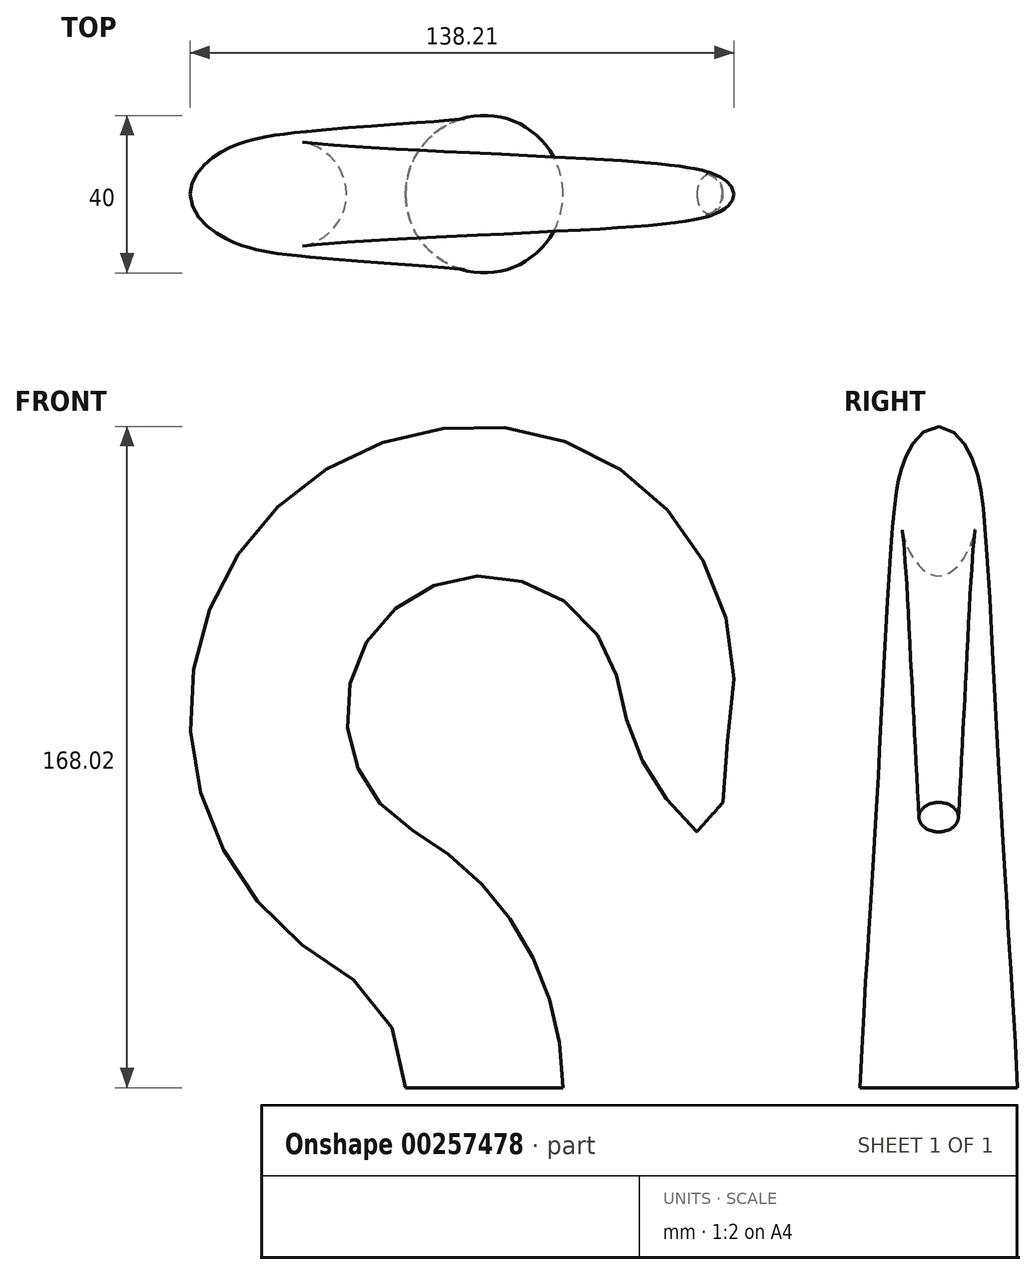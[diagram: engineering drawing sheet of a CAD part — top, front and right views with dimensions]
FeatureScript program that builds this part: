
annotation { "Feature Type Name" : "Feature", "Feature Type Description" : "" }
export const myFeature = defineFeature(function(context is Context, id is Id, definition is map)
    precondition{}
    {
        {
            var Q0;
            Q0=qCreatedBy(makeId("Front.planeOp"),FACE);
            var sketch = newSketch(context, id + "F0", { "sketchPlane" : qUnion([Q0])});
            skLineSegment(sketch, "E0", {"start": v(0, 0) * mm, "end": v(-40, 0) * mm});
            skPoint(sketch, "E1", {"position": v(-20, 0) * mm});
            skLineSegment(sketch, "E2", {"start": v(-20, 0) * mm, "end": v(-20, 168) * mm, "construction": true});
            skArc(sketch, "E3", {"start": v(-40, 0) * mm, "mid": v(-44.68, 17.48) * mm, "end": v(-57.46, 30.29) * mm});
            skArc(sketch, "E4", {"start": v(0, 0) * mm, "mid": v(-10.1, 37.58) * mm, "end": v(-37.66, 65.04) * mm});
            skLineSegment(sketch, "E5", {"start": v(-131.2, 95) * mm, "end": v(85.23, 95) * mm, "construction": true});
            skArc(sketch, "E6", {"start": v(-57.46, 30.29) * mm, "mid": v(-84.78, 57.65) * mm, "end": v(-94.77, 95) * mm});
            skArc(sketch, "E7", {"start": v(-55, 95) * mm, "mid": v(-44.75, 119.75) * mm, "end": v(-20, 130) * mm});
            skArc(sketch, "E8", {"start": v(-37.66, 65.04) * mm, "mid": v(-50.35, 77.7) * mm, "end": v(-55, 95) * mm});
            skArc(sketch, "E9", {"start": v(41.75, 88.29) * mm, "mid": v(29.83, 142.83) * mm, "end": v(-20, 168) * mm});
            skArc(sketch, "E10", {"start": v(41.75, 88.29) * mm, "mid": v(40.57, 80.43) * mm, "end": v(40.65, 72.48) * mm});
            skLineSegment(sketch, "E11", {"start": v(40.65, 72.48) * mm, "end": v(34.02, 65) * mm});
            skCircle(sketch, "E12", {"center": v(37.33, 68.74) * mm, "radius": 5 * mm, "construction": true});
            skArc(sketch, "E13", {"start": v(34.02, 65) * mm, "mid": v(21.2, 81.05) * mm, "end": v(14.57, 100.49) * mm});
            skArc(sketch, "E14", {"start": v(-20, 130) * mm, "mid": v(2.73, 121.62) * mm, "end": v(14.57, 100.49) * mm});
            skArc(sketch, "E15", {"start": v(-94.77, 95) * mm, "mid": v(-72.76, 147.25) * mm, "end": v(-20, 168) * mm});
            skSolve(sketch);
        }
        {
            var Q0;
            Q0=qCreatedBy(makeId("Top.planeOp"),FACE);
            var sketch = newSketch(context, id + "F1", { "sketchPlane" : qUnion([Q0])});
            skPoint(sketch, "E16.0", {"position": v(-20, 0) * mm});
            skPoint(sketch, "E17.0", {"position": v(-40, 0) * mm});
            skCircle(sketch, "E18", {"center": v(-20, 0) * mm, "radius": 20 * mm});
            skSolve(sketch);
        }
        {
            var Q0;
            Q0=sQuery(id+"F0.wireOp",EDGE,"E11");
            cPlane(context, id + "F2", {"entities" : qUnion([Q0]), "cplaneType" : CPlaneType.LINE_ANGLE, "offset" : 25 * mm, "angle" : 0 * degree, "width" : 150 * mm, "height" : 150 * mm});
        }
        {
            var Q0;
            Q0=qCreatedBy(id+"F2.planeOp",FACE);
            var sketch = newSketch(context, id + "F3", { "sketchPlane" : qUnion([Q0])});
            skLineSegment(sketch, "E19.0", {"start": v(0, 81.2) * mm, "end": v(0, 71.2) * mm, "construction": true});
            skCircle(sketch, "E20", {"center": v(0, 76.2) * mm, "radius": 5 * mm});
            skSolve(sketch);
        }
        {
            var Q0;
            Q0=qCreatedBy(makeId("Front.planeOp"),FACE);
            var sketch = newSketch(context, id + "F4", { "sketchPlane" : qUnion([Q0])});
            skArc(sketch, "E21.0", {"start": v(-40, 0) * mm, "mid": v(-44.68, 17.48) * mm, "end": v(-57.46, 30.29) * mm});
            skArc(sketch, "E22.0", {"start": v(-57.46, 30.29) * mm, "mid": v(-84.78, 57.65) * mm, "end": v(-94.77, 95) * mm});
            skArc(sketch, "E23.0", {"start": v(-94.77, 95) * mm, "mid": v(-72.76, 147.25) * mm, "end": v(-20, 168) * mm});
            skArc(sketch, "E24.0", {"start": v(41.75, 88.29) * mm, "mid": v(29.83, 142.83) * mm, "end": v(-20, 168) * mm});
            skArc(sketch, "E25.0", {"start": v(41.75, 88.29) * mm, "mid": v(40.57, 80.43) * mm, "end": v(40.65, 72.48) * mm});
            skSolve(sketch);
        }
        {
            var Q0;
            Q0=qCreatedBy(makeId("Front.planeOp"),FACE);
            var sketch = newSketch(context, id + "F5", { "sketchPlane" : qUnion([Q0])});
            skArc(sketch, "E26.0", {"start": v(0, 0) * mm, "mid": v(-10.1, 37.58) * mm, "end": v(-37.66, 65.04) * mm});
            skArc(sketch, "E27.0", {"start": v(-37.66, 65.04) * mm, "mid": v(-50.35, 77.7) * mm, "end": v(-55, 95) * mm});
            skArc(sketch, "E28.0", {"start": v(-55, 95) * mm, "mid": v(-44.75, 119.75) * mm, "end": v(-20, 130) * mm});
            skArc(sketch, "E29.0", {"start": v(-20, 130) * mm, "mid": v(2.73, 121.62) * mm, "end": v(14.57, 100.49) * mm});
            skArc(sketch, "E30.0", {"start": v(34.02, 65) * mm, "mid": v(21.2, 81.05) * mm, "end": v(14.57, 100.49) * mm});
            skSolve(sketch);
        }
        {
            var Q0;
            Q0=makeQuery(id+"F1.imprint","IMPRINT",FACE,{"disambiguationData":[TD([[makeQuery(id+"F1.imprint","IMPRINT",EDGE,{"derivedFrom":sQuery(id+"F1.wireOp",EDGE,"E18")}),1.0]])]});
            var Q1;
            Q1=makeQuery(id+"F3.imprint","IMPRINT",FACE,{"disambiguationData":[TD([[makeQuery(id+"F3.imprint","IMPRINT",EDGE,{"derivedFrom":sQuery(id+"F3.wireOp",EDGE,"E20")}),1.0]])]});
            var Q2;
            Q2 = qConstructionFilter(qBodyType(qCreatedBy(id + "F4" ,EDGE), BodyType.WIRE), ConstructionObject.NO);
            var Q3;
            Q3 = qConstructionFilter(qBodyType(qCreatedBy(id + "F5" ,EDGE), BodyType.WIRE), ConstructionObject.NO);
            loft(context, id + "F6", {"addGuides" : true, "sheetProfilesArray" : [{ "sheetProfileEntities" : qUnion([Q0]) }, { "sheetProfileEntities" : qUnion([Q1]) }], "guidesArray" : [{ "guideEntities" : qUnion([Q2]), "guideDerivativeType" : LoftGuideDerivativeType.DEFAULT, "guideDerivativeMagnitude" : 1 }, { "guideEntities" : qUnion([Q3]), "guideDerivativeType" : LoftGuideDerivativeType.DEFAULT, "guideDerivativeMagnitude" : 1 }]});
        }
    });
